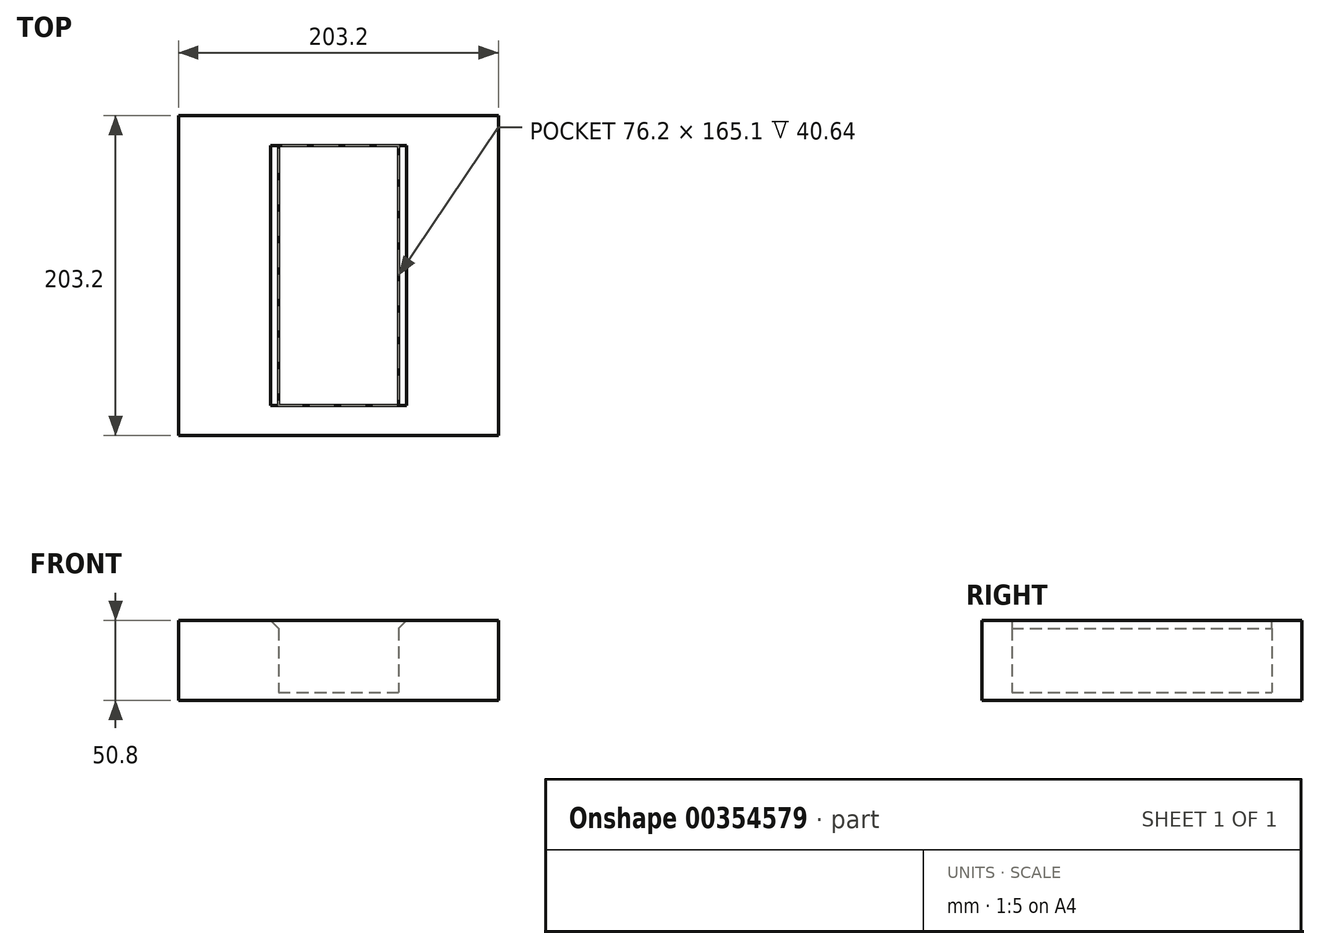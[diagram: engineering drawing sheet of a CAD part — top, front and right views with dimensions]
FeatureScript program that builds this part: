
annotation { "Feature Type Name" : "Feature", "Feature Type Description" : "" }
export const myFeature = defineFeature(function(context is Context, id is Id, definition is map)
    precondition{}
    {
        {
            var Q0;
            Q0=qCreatedBy(makeId("Top.planeOp"),FACE);
            var sketch = newSketch(context, id + "F0", { "sketchPlane" : qUnion([Q0])});
            skLineSegment(sketch, "E0.bottom", {"start": v(101.6, 101.6) * mm, "end": v(-101.6, 101.6) * mm});
            skLineSegment(sketch, "E0.top", {"start": v(101.6, -101.6) * mm, "end": v(-101.6, -101.6) * mm});
            skLineSegment(sketch, "E0.left", {"start": v(101.6, 101.6) * mm, "end": v(101.6, -101.6) * mm});
            skLineSegment(sketch, "E0.right", {"start": v(-101.6, 101.6) * mm, "end": v(-101.6, -101.6) * mm});
            skPoint(sketch, "E0.middle", {"position": v(0, 0) * mm});
            skLineSegment(sketch, "E1.bottom", {"start": v(38.1, 82.55) * mm, "end": v(-38.1, 82.55) * mm});
            skLineSegment(sketch, "E1.top", {"start": v(38.1, -82.55) * mm, "end": v(-38.1, -82.55) * mm});
            skLineSegment(sketch, "E1.left", {"start": v(38.1, 82.55) * mm, "end": v(38.1, -82.55) * mm});
            skLineSegment(sketch, "E1.right", {"start": v(-38.1, 82.55) * mm, "end": v(-38.1, -82.55) * mm});
            skSolve(sketch);
        }
        {
            var Q0;
            Q0=makeQuery(id+"F0.imprint","IMPRINT",FACE,{"disambiguationData":[TD([[makeQuery(id+"F0.imprint","IMPRINT",EDGE,{"derivedFrom":sQuery(id+"F0.wireOp",EDGE,"E0.bottom")}),1.0]])]});
            var Q1;
            Q1=makeQuery(id+"F0.imprint","IMPRINT",FACE,{"disambiguationData":[TD([[makeQuery(id+"F0.imprint","IMPRINT",EDGE,{"derivedFrom":sQuery(id+"F0.wireOp",EDGE,"E1.bottom")}),1.0]])]});
            extrude(context, id + "F1", {"entities" : qUnion([Q0, Q1]), "depth" : 5.08 * mm});
        }
        {
            var Q0;
            Q0=makeQuery(id+"F0.imprint","IMPRINT",FACE,{"disambiguationData":[TD([[makeQuery(id+"F0.imprint","IMPRINT",EDGE,{"derivedFrom":sQuery(id+"F0.wireOp",EDGE,"E0.bottom")}),1.0]])]});
            extrude(context, id + "F2", {"entities" : qUnion([Q0]), "operationType" : NewBodyOperationType.ADD, "depth" : 50.8 * mm});
        }
        {
            var Q0;
            Q0=makeQuery(id+"F2.opExtrude","CAP_EDGE",EDGE,{"disambiguationData":[OSD([sQuery(id+"F0.wireOp",EDGE,"E1.right")])],"isStart":false});
            var Q1;
            Q1=makeQuery(id+"F2.opExtrude","CAP_EDGE",EDGE,{"disambiguationData":[OSD([sQuery(id+"F0.wireOp",EDGE,"E1.left")])],"isStart":false});
            var Q2;
            Q2=makeQuery(id+"Fp5J9ZUWkjBt794_1.boolean.opBoolean","COPY",EDGE,{"derivedFrom":makeQuery(id+"Fp5J9ZUWkjBt794_1.opExtrude","CAP_EDGE",EDGE,{"disambiguationData":[OSD([sQuery(id+"FsXzQ7LTdRUKm0j_1.wireOp",EDGE,"fSqhZmvi-Lejk-lD7R-YKzu-Np0E2h53vfxE")])],"isStart":true})});
            chamfer(context, id + "F3", {"entities" : qUnion([Q0, Q1, Q2]), "width" : 5.08 * mm, "tangentPropagation" : true});
        }
    });
